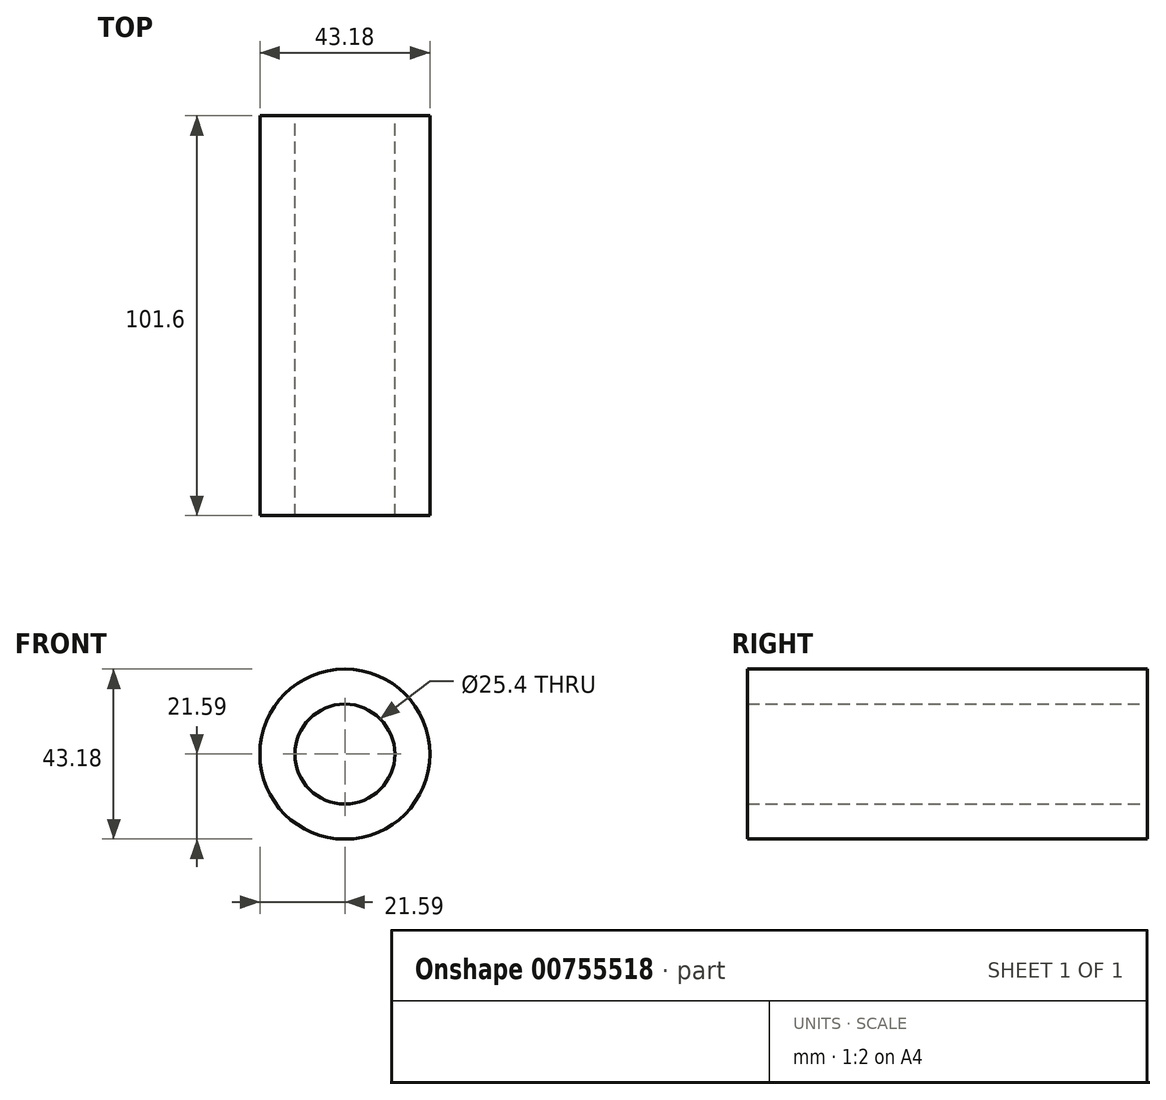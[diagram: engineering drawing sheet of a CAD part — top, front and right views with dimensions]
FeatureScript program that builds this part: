
annotation { "Feature Type Name" : "Feature", "Feature Type Description" : "" }
export const myFeature = defineFeature(function(context is Context, id is Id, definition is map)
    precondition{}
    {
        {
            var Q0;
            Q0=qCreatedBy(makeId("Front.planeOp"),FACE);
            var sketch = newSketch(context, id + "F0", { "sketchPlane" : qUnion([Q0])});
            skCircle(sketch, "E0", {"center": v(0, 0) * mm, "radius": 21.59 * mm});
            skCircle(sketch, "E1", {"center": v(0, 0) * mm, "radius": 12.7 * mm});
            skSolve(sketch);
        }
        {
            var Q0;
            Q0 = qSketchRegion(id + "F0", true);
            extrude(context, id + "F1", {"entities" : qUnion([Q0]), "depth" : 101.6 * mm, "offsetDistance" : 25.4 * mm});
        }
        {
            var Q0;
            Q0=qCreatedBy(makeId("Right.planeOp"),FACE);
            var sketch = newSketch(context, id + "F2", { "sketchPlane" : qUnion([Q0])});
            skCircle(sketch, "E2", {"center": v(121.5, 119.55) * mm, "radius": 12.7 * mm});
            skSolve(sketch);
        }
        {
            var Q0;
            Q0 = qBodyType(qCreatedBy(id + "F2" ,EDGE), BodyType.WIRE);
            var Q1;
            Q1=sQuery(id+"F2.wireOp",EDGE,"E2");
            extrude(context, id + "F3", {"bodyType" : ToolBodyType.SURFACE, "surfaceEntities" : qUnion([Q0, Q1]), "depth" : 254 * mm, "offsetDistance" : 25.4 * mm});
        }
    });
